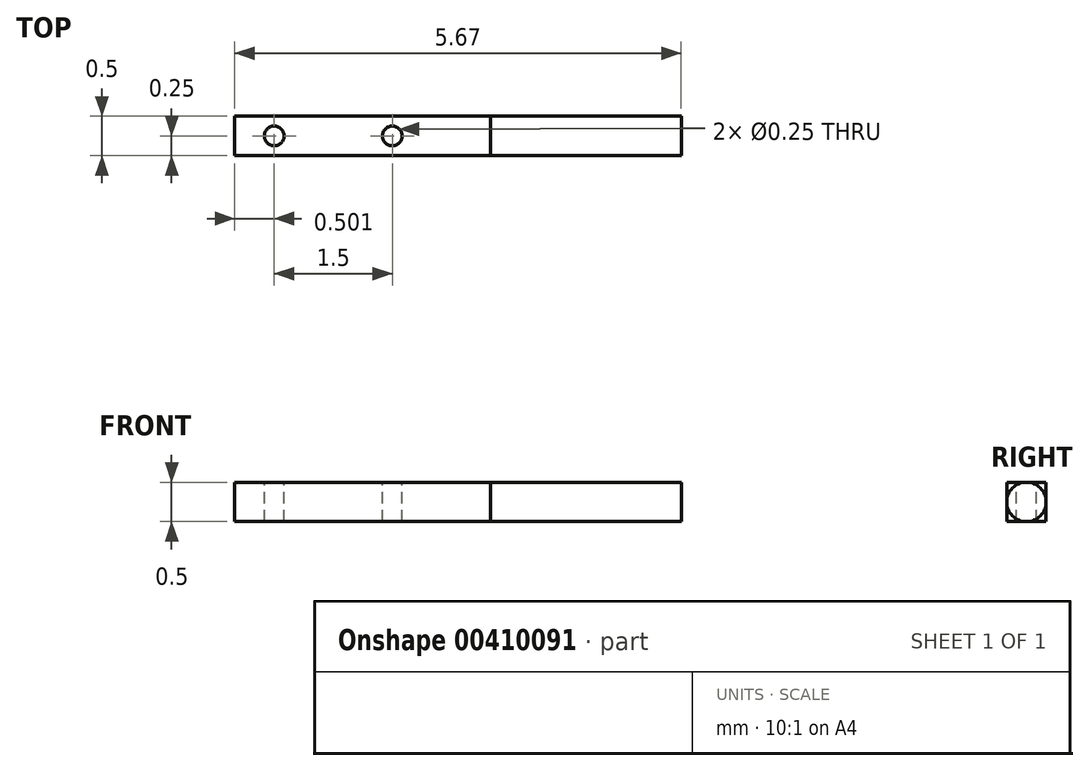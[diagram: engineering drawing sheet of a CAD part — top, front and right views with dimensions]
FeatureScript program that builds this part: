
annotation { "Feature Type Name" : "Feature", "Feature Type Description" : "" }
export const myFeature = defineFeature(function(context is Context, id is Id, definition is map)
    precondition{}
    {
        {
            var Q0;
            Q0=qCreatedBy(makeId("Front.planeOp"),FACE);
            var sketch = newSketch(context, id + "F0", { "sketchPlane" : qUnion([Q0])});
            skLineSegment(sketch, "E0.bottom", {"start": v(0, 0.25) * mm, "end": v(-3.25, 0.25) * mm});
            skLineSegment(sketch, "E0.top", {"start": v(0, -0.25) * mm, "end": v(-3.25, -0.25) * mm});
            skLineSegment(sketch, "E0.left", {"start": v(0, 0.25) * mm, "end": v(0, -0.25) * mm});
            skLineSegment(sketch, "E0.right", {"start": v(-3.25, 0.25) * mm, "end": v(-3.25, -0.25) * mm});
            skLineSegment(sketch, "E1.bottom", {"start": v(0, 0) * mm, "end": v(2.42, 0) * mm});
            skLineSegment(sketch, "E1.top", {"start": v(0, 0.25) * mm, "end": v(2.42, 0.25) * mm});
            skLineSegment(sketch, "E1.left", {"start": v(0, 0) * mm, "end": v(0, 0.25) * mm});
            skLineSegment(sketch, "E1.right", {"start": v(2.42, 0) * mm, "end": v(2.42, 0.25) * mm});
            skSolve(sketch);
        }
        {
            var Q0;
            Q0=makeQuery(id+"F0.imprint","IMPRINT",FACE,{"disambiguationData":[TD([[makeQuery(id+"F0.imprint","IMPRINT",EDGE,{"derivedFrom":sQuery(id+"F0.wireOp",EDGE,"E0.bottom")}),1.0]])]});
            extrude(context, id + "F1", {"entities" : qUnion([Q0]), "endBound" : BoundingType.SYMMETRIC, "depth" : 0.5 * mm});
        }
        {
            var Q0;
            Q0=makeQuery(id+"F0.imprint","IMPRINT",FACE,{"disambiguationData":[TD([[makeQuery(id+"F0.imprint","IMPRINT",EDGE,{"derivedFrom":sQuery(id+"F0.wireOp",EDGE,"E1.bottom")}),1.0]])]});
            var Q1;
            Q1=sQuery(id+"F0.wireOp",EDGE,"E1.bottom");
            revolve(context, id + "F2", {"operationType" : NewBodyOperationType.ADD, "entities" : qUnion([Q0]), "axis" : qUnion([Q1]), "revolveType" : RevolveType.FULL});
        }
        {
            var Q0;
            Q0=makeQuery(id+"F1.opExtrude","SWEPT_FACE",FACE,{"disambiguationData":[OSD([sQuery(id+"F0.wireOp",EDGE,"E0.bottom")])]});
            var sketch = newSketch(context, id + "F3", { "sketchPlane" : qUnion([Q0])});
            skCircle(sketch, "E2", {"center": v(-2.75, 0) * mm, "radius": 0.12 * mm});
            skCircle(sketch, "E3", {"center": v(-1.25, 0) * mm, "radius": 0.12 * mm});
            skSolve(sketch);
        }
        {
            var Q0;
            Q0 = qSketchRegion(id + "F3", true);
            extrude(context, id + "F4", {"entities" : qUnion([Q0]), "operationType" : NewBodyOperationType.REMOVE, "endBound" : BoundingType.THROUGH_ALL, "oppositeDirection" : true, "depth" : 25 * mm});
        }
    });
